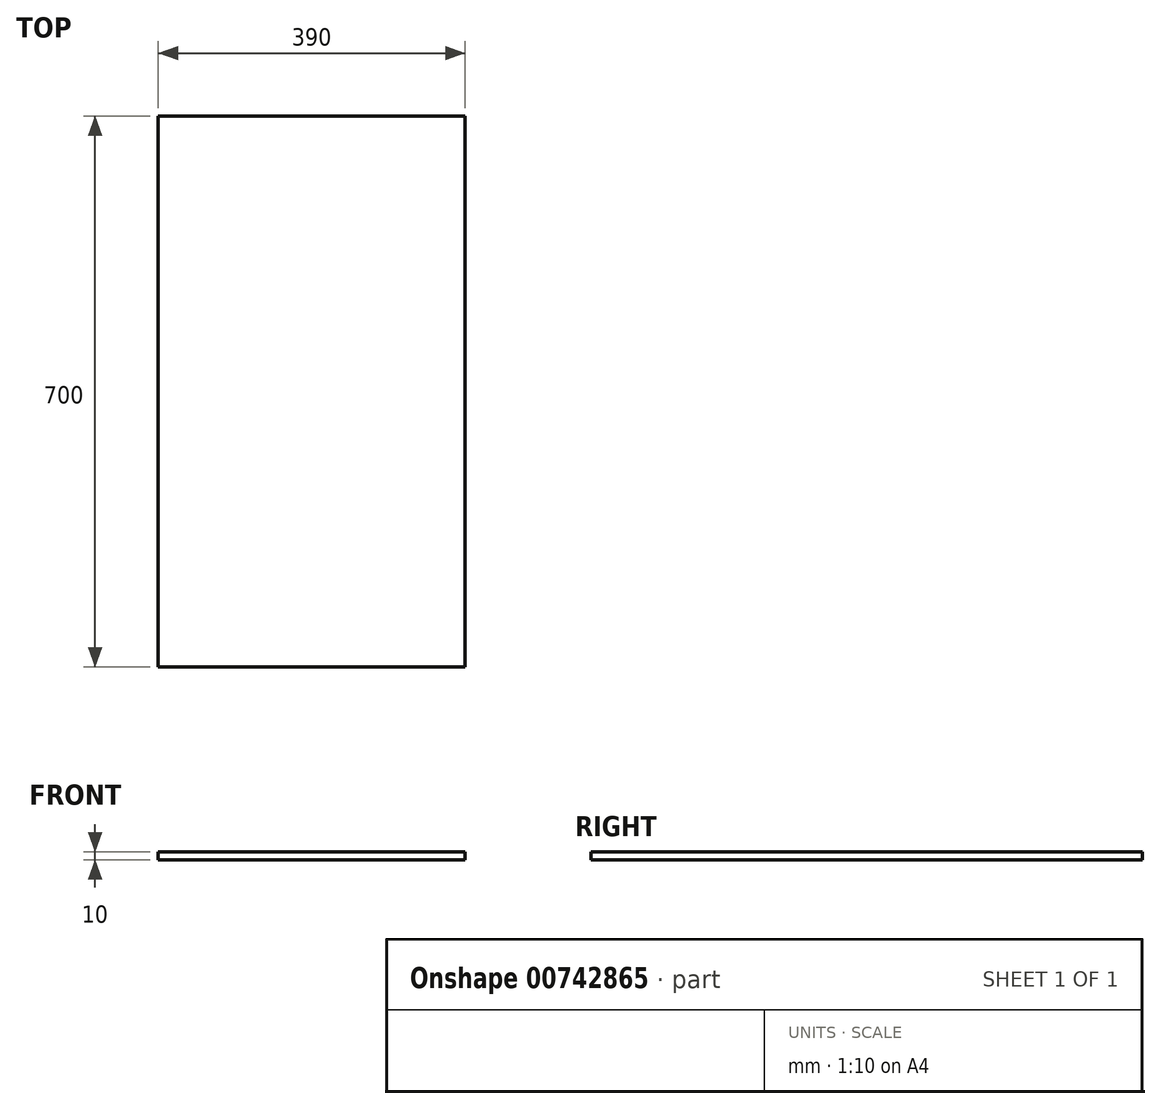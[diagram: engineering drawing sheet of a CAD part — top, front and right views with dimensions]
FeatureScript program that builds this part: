
annotation { "Feature Type Name" : "Feature", "Feature Type Description" : "" }
export const myFeature = defineFeature(function(context is Context, id is Id, definition is map)
    precondition{}
    {
        {
            var Q0;
            Q0=qCreatedBy(makeId("Top.planeOp"),FACE);
            var sketch = newSketch(context, id + "F0", { "sketchPlane" : qUnion([Q0])});
            skLineSegment(sketch, "E0.bottom", {"start": v(195, 350) * mm, "end": v(-195, 350) * mm});
            skLineSegment(sketch, "E0.top", {"start": v(195, -350) * mm, "end": v(-195, -350) * mm});
            skLineSegment(sketch, "E0.left", {"start": v(195, 350) * mm, "end": v(195, -350) * mm});
            skLineSegment(sketch, "E0.right", {"start": v(-195, 350) * mm, "end": v(-195, -350) * mm});
            skPoint(sketch, "E0.middle", {"position": v(0, 0) * mm});
            skSolve(sketch);
        }
        {
            var Q0;
            Q0 = qSketchRegion(id + "F0", true);
            extrude(context, id + "F1", {"entities" : qUnion([Q0]), "endBound" : BoundingType.SYMMETRIC, "depth" : 10 * mm, "offsetDistance" : 25.4 * mm});
        }
    });
